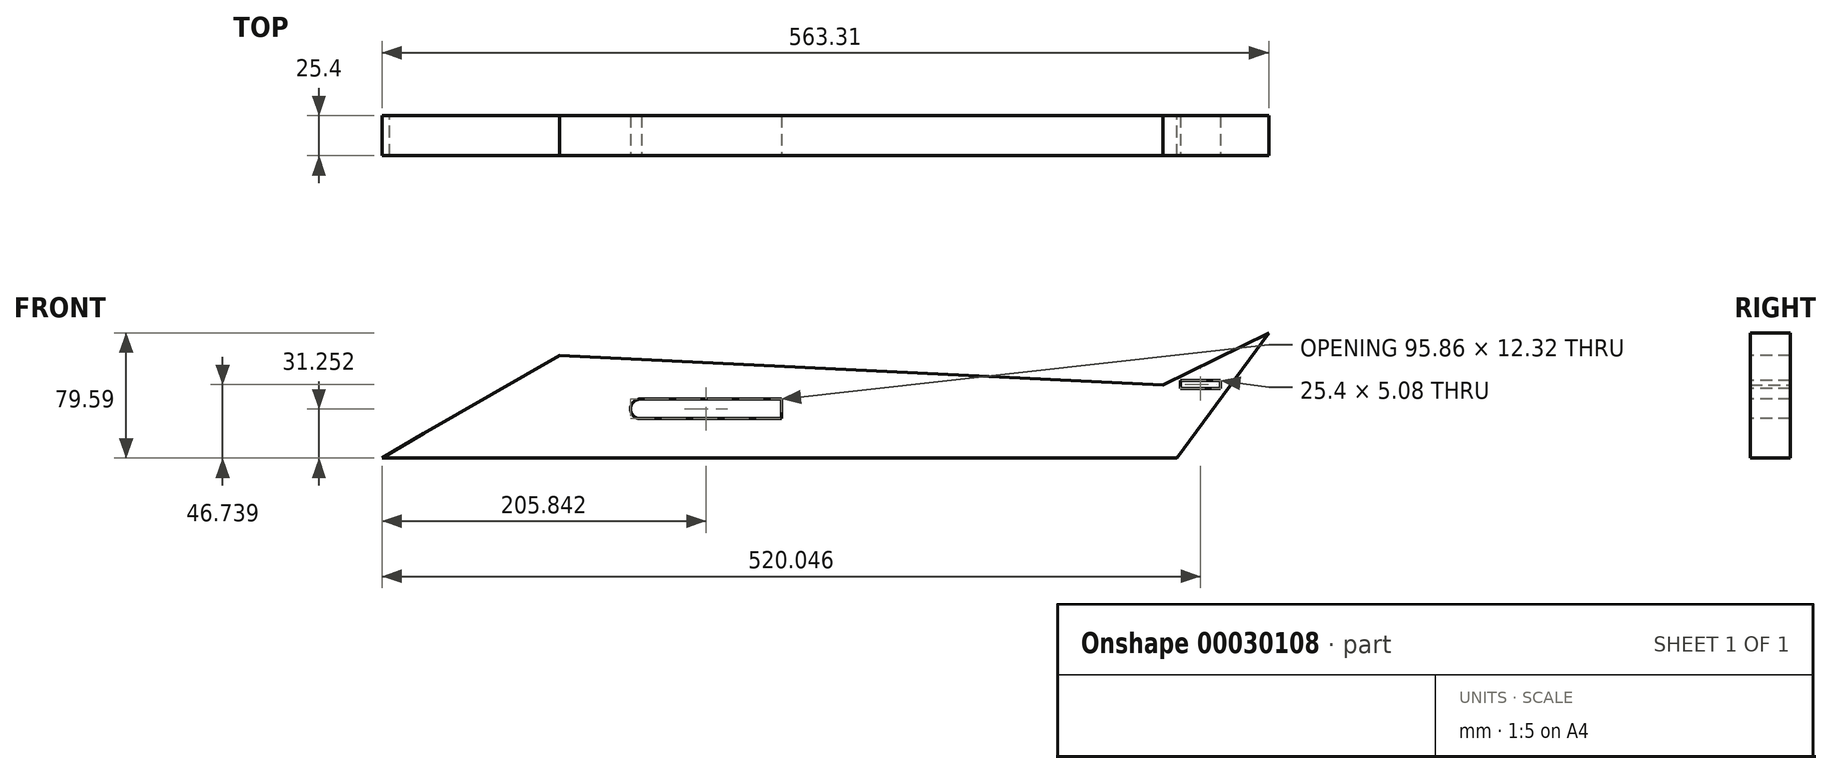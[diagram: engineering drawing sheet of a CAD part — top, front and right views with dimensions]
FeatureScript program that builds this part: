
annotation { "Feature Type Name" : "Feature", "Feature Type Description" : "" }
export const myFeature = defineFeature(function(context is Context, id is Id, definition is map)
    precondition{}
    {
        {
            var Q0;
            Q0=qCreatedBy(makeId("Front.planeOp"),FACE);
            var sketch = newSketch(context, id + "F0", { "sketchPlane" : qUnion([Q0])});
            skLineSegment(sketch, "E0", {"start": v(-248.94, -25.05) * mm, "end": v(251.06, -25.05) * mm});
            skLineSegment(sketch, "E1", {"start": v(251.06, -25.05) * mm, "end": v(309.54, 54.5) * mm});
            skLineSegment(sketch, "E2", {"start": v(309.54, 54.5) * mm, "end": v(242.29, 21.36) * mm});
            skLineSegment(sketch, "E3", {"start": v(242.29, 21.36) * mm, "end": v(-248.94, 45.48) * mm});
            skArc(sketch, "E4", {"start": v(-248.94, 45.48) * mm, "mid": v(-285.98, 10.21) * mm, "end": v(-248.94, -25.05) * mm});
            skSolve(sketch);
        }
        {
            var Q0;
            Q0=makeQuery(id+"F0.imprint","IMPRINT",FACE,{"disambiguationData":[TD([[makeQuery(id+"F0.imprint","IMPRINT",EDGE,{"derivedFrom":sQuery(id+"F0.wireOp",EDGE,"E0")}),1.0]])]});
            extrude(context, id + "F1", {"entities" : qUnion([Q0]), "depth" : 25.4 * mm});
        }
        {
            var Q0;
            Q0 = qSketchRegion(id + "F0", true);
            extrude(context, id + "F2", {"entities" : qUnion([Q0]), "operationType" : NewBodyOperationType.ADD, "depth" : 25.4 * mm});
        }
        {
            var Q0;
            Q0 = qSketchRegion(id + "F0", true);
            extrude(context, id + "F3", {"entities" : qUnion([Q0]), "operationType" : NewBodyOperationType.ADD, "depth" : 25.4 * mm});
        }
        {
            var Q0;
            Q0=makeQuery(id+"F1.opExtrude","CAP_FACE",FACE,{"disambiguationData":[OSD([sQuery(id+"F0.wireOp",EDGE,"E0"),sQuery(id+"F0.wireOp",EDGE,"E1"),sQuery(id+"F0.wireOp",EDGE,"E2"),sQuery(id+"F0.wireOp",EDGE,"E3"),sQuery(id+"F0.wireOp",EDGE,"E4")])],"isStart":false});
            var sketch = newSketch(context, id + "F4", { "sketchPlane" : qUnion([Q0])});
            skLineSegment(sketch, "E5", {"start": v(-88.78, 0) * mm, "end": v(0, 0) * mm});
            skLineSegment(sketch, "E6", {"start": v(0, 0) * mm, "end": v(-88.78, 12.32) * mm});
            skArc(sketch, "E7", {"start": v(-88.78, 12.32) * mm, "mid": v(-95.86, 6.16) * mm, "end": v(-88.78, 0) * mm});
            skSolve(sketch);
        }
        {
            var Q0;
            Q0=makeQuery(id+"F4.imprint","IMPRINT",FACE,{"disambiguationData":[TD([[makeQuery(id+"F4.imprint","IMPRINT",EDGE,{"derivedFrom":sQuery(id+"F4.wireOp",EDGE,"E5")}),1.0]])]});
            extrude(context, id + "F5", {"entities" : qUnion([Q0]), "operationType" : NewBodyOperationType.REMOVE, "oppositeDirection" : true, "depth" : 25.4 * mm});
        }
        {
            var Q0;
            Q0=makeQuery(id+"F1.opExtrude","CAP_FACE",FACE,{"disambiguationData":[OSD([sQuery(id+"F0.wireOp",EDGE,"E0"),sQuery(id+"F0.wireOp",EDGE,"E1"),sQuery(id+"F0.wireOp",EDGE,"E2"),sQuery(id+"F0.wireOp",EDGE,"E3"),sQuery(id+"F0.wireOp",EDGE,"E4")])],"isStart":false});
            var sketch = newSketch(context, id + "F6", { "sketchPlane" : qUnion([Q0])});
            skLineSegment(sketch, "E8", {"start": v(-88.78, 12.32) * mm, "end": v(-88.78, 0) * mm});
            skLineSegment(sketch, "E9", {"start": v(-88.78, 12.32) * mm, "end": v(0, 12.32) * mm});
            skLineSegment(sketch, "E10", {"start": v(0, 12.32) * mm, "end": v(0, 0) * mm});
            skSolve(sketch);
        }
        {
            var Q0;
            Q0 = qSketchRegion(id + "F6", true);
            var Q1;
            Q1=makeQuery(id+"F6.imprint","IMPRINT",FACE,{"disambiguationData":[TD([[makeQuery(id+"F6.imprint","IMPRINT",EDGE,{"derivedFrom":sQuery(id+"F6.wireOp",EDGE,"E8")}),1.0]])]});
            var Q2;
            Q2=makeQuery(id+"F6.imprint","IMPRINT",FACE,{"disambiguationData":[TD([[makeQuery(id+"F6.imprint","IMPRINT",EDGE,{"derivedFrom":sQuery(id+"F6.wireOp",EDGE,"E9")}),-1.0]])]});
            extrude(context, id + "F7", {"entities" : qUnion([Q0, Q1, Q2]), "operationType" : NewBodyOperationType.REMOVE, "oppositeDirection" : true, "depth" : 25.4 * mm});
        }
        {
            var Q0;
            Q0=makeQuery(id+"F1.opExtrude","CAP_FACE",FACE,{"disambiguationData":[OSD([sQuery(id+"F0.wireOp",EDGE,"E0"),sQuery(id+"F0.wireOp",EDGE,"E1"),sQuery(id+"F0.wireOp",EDGE,"E2"),sQuery(id+"F0.wireOp",EDGE,"E3"),sQuery(id+"F0.wireOp",EDGE,"E4")])],"isStart":false});
            var sketch = newSketch(context, id + "F8", { "sketchPlane" : qUnion([Q0])});
            skLineSegment(sketch, "E11", {"start": v(-88.78, 12.32) * mm, "end": v(-88.78, 0) * mm});
            skSolve(sketch);
        }
        {
            var Q0;
            Q0 = qSketchRegion(id + "F8", true);
            var Q1;
            Q1=makeQuery(id+"F8.imprint","IMPRINT",FACE,{"disambiguationData":[TD([[makeQuery(id+"F8.imprint","IMPRINT",EDGE,{"derivedFrom":sQuery(id+"F8.wireOp",EDGE,"E11")}),-1.0]])]});
            extrude(context, id + "F9", {"entities" : qUnion([Q0, Q1]), "depth" : 25.4 * mm});
        }
        {
            var Q0;
            Q0=makeQuery(id+"F9.opExtrude","CAP_FACE",FACE,{"disambiguationData":[OSD([sQuery(id+"F4.wireOp",EDGE,"E7"),sQuery(id+"F8.wireOp",EDGE,"E11")])],"isStart":false});
            extrude(context, id + "F10", {"entities" : qUnion([Q0]), "operationType" : NewBodyOperationType.REMOVE, "oppositeDirection" : true, "depth" : 25.4 * mm});
        }
        {
            var Q0;
            Q0=makeQuery(id+"F1.opExtrude","CAP_FACE",FACE,{"disambiguationData":[OSD([sQuery(id+"F0.wireOp",EDGE,"E0"),sQuery(id+"F0.wireOp",EDGE,"E1"),sQuery(id+"F0.wireOp",EDGE,"E2"),sQuery(id+"F0.wireOp",EDGE,"E3"),sQuery(id+"F0.wireOp",EDGE,"E4")])],"isStart":false});
            var sketch = newSketch(context, id + "F11", { "sketchPlane" : qUnion([Q0])});
            skLineSegment(sketch, "E12.bottom", {"start": v(-88.78, -10.1) * mm, "end": v(-110.2, -10.1) * mm});
            skLineSegment(sketch, "E12.top", {"start": v(-88.78, 19.23) * mm, "end": v(-110.2, 19.23) * mm});
            skLineSegment(sketch, "E12.left", {"start": v(-88.78, -10.1) * mm, "end": v(-88.78, 19.23) * mm});
            skLineSegment(sketch, "E12.right", {"start": v(-110.2, -10.1) * mm, "end": v(-110.2, 19.23) * mm});
            skSolve(sketch);
        }
        {
            var Q0;
            {var subQ0=makeQuery(id+"F5.boolean.opBoolean","COPY",EDGE,{"derivedFrom":makeQuery(id+"F5.opExtrude","CAP_EDGE",EDGE,{"disambiguationData":[OSD([sQuery(id+"F4.wireOp",EDGE,"E7")])],"isStart":true})});Q0=makeQuery(id+"F11.imprint","IMPRINT",FACE,{"disambiguationData":[TD([[makeQuery(id+"F11.imprint","IMPRINT",EDGE,{"derivedFrom":subQ0}),1.0]])]});}
            var Q1;
            {var subQ1=sQuery(id+"F11.wireOp",EDGE,"E12.bottom");Q1=makeQuery(id+"F11.imprint","IMPRINT",FACE,{"disambiguationData":[TD([[makeQuery(id+"F11.imprint","IMPRINT",EDGE,{"derivedFrom":subQ1}),-1.0]])]});}
            extrude(context, id + "F12", {"entities" : qUnion([Q0, Q1]), "operationType" : NewBodyOperationType.ADD, "oppositeDirection" : true, "depth" : 25.4 * mm});
        }
        {
            var Q0;
            Q0=makeQuery(id+"F12.boolean.opBoolean","MERGE",FACE,{"derivedFrom":[makeQuery(id+"F1.opExtrude","CAP_FACE",FACE,{"disambiguationData":[OSD([sQuery(id+"F0.wireOp",EDGE,"E0"),sQuery(id+"F0.wireOp",EDGE,"E1"),sQuery(id+"F0.wireOp",EDGE,"E2"),sQuery(id+"F0.wireOp",EDGE,"E3"),sQuery(id+"F0.wireOp",EDGE,"E4")])],"isStart":false}),makeQuery(id+"F12.opExtrude","CAP_FACE",FACE,{"disambiguationData":[OSD([sQuery(id+"F11.wireOp",EDGE,"E12.bottom"),sQuery(id+"F11.wireOp",EDGE,"E12.top"),sQuery(id+"F11.wireOp",EDGE,"E12.left"),sQuery(id+"F11.wireOp",EDGE,"E12.right")])],"isStart":true})]});
            var sketch = newSketch(context, id + "F13", { "sketchPlane" : qUnion([Q0])});
            skLineSegment(sketch, "E13", {"start": v(-248.94, -25.05) * mm, "end": v(-130.9, 39.68) * mm});
            skSolve(sketch);
        }
        {
            var Q0;
            Q0=makeQuery(id+"F1.opExtrude","CAP_FACE",FACE,{"disambiguationData":[OSD([sQuery(id+"F0.wireOp",EDGE,"E0"),sQuery(id+"F0.wireOp",EDGE,"E1"),sQuery(id+"F0.wireOp",EDGE,"E2"),sQuery(id+"F0.wireOp",EDGE,"E3"),sQuery(id+"F0.wireOp",EDGE,"E4")])],"isStart":false});
            var sketch = newSketch(context, id + "F14", { "sketchPlane" : qUnion([Q0])});
            skSolve(sketch);
        }
        {
            var Q0;
            {var subQ1=sQuery(id+"F13.wireOp",EDGE,"E13");Q0=makeQuery(id+"F13.imprint","IMPRINT",FACE,{"disambiguationData":[TD([[makeQuery(id+"F13.imprint","IMPRINT",EDGE,{"derivedFrom":subQ1}),1.0]])]});}
            extrude(context, id + "F15", {"entities" : qUnion([Q0]), "operationType" : NewBodyOperationType.ADD, "depth" : 25.4 * mm});
        }
        {
            var Q0;
            Q0=makeQuery(id+"F15.opExtrude","CAP_FACE",FACE,{"disambiguationData":[OSD([sQuery(id+"F0.wireOp",EDGE,"E3"),sQuery(id+"F0.wireOp",EDGE,"E4"),sQuery(id+"F13.wireOp",EDGE,"E13")])],"isStart":false});
            extrude(context, id + "F16", {"entities" : qUnion([Q0]), "operationType" : NewBodyOperationType.REMOVE, "oppositeDirection" : true, "depth" : 25.4 * mm});
        }
        {
            var Q0;
            Q0=makeQuery(id+"F14.imprint","IMPRINT",FACE,{"disambiguationData":[TD([[makeQuery(id+"F14.imprint","IMPRINT",EDGE,{"derivedFrom":makeQuery(id+"F1.opExtrude","CAP_EDGE",EDGE,{"disambiguationData":[OSD([sQuery(id+"F0.wireOp",EDGE,"E0")])],"isStart":false})}),1.0]])]});
            var sketch = newSketch(context, id + "F17", { "sketchPlane" : qUnion([Q0])});
            skLineSegment(sketch, "E14", {"start": v(-255.34, -25.8) * mm, "end": v(-138.7, 41.46) * mm});
            skLineSegment(sketch, "E15", {"start": v(-138.7, 41.46) * mm, "end": v(-278.67, 55.02) * mm});
            skLineSegment(sketch, "E16", {"start": v(-278.67, 55.02) * mm, "end": v(-310.47, -22.74) * mm});
            skLineSegment(sketch, "E17", {"start": v(-310.47, -22.74) * mm, "end": v(-255.34, -25.8) * mm});
            skSolve(sketch);
        }
        {
            var Q0;
            Q0 = qSketchRegion(id + "F17", true);
            extrude(context, id + "F18", {"entities" : qUnion([Q0]), "operationType" : NewBodyOperationType.REMOVE, "oppositeDirection" : true, "depth" : 25.4 * mm});
        }
        {
            var Q0;
            Q0=makeQuery(id+"F14.imprint","IMPRINT",FACE,{"disambiguationData":[TD([[makeQuery(id+"F14.imprint","IMPRINT",EDGE,{"derivedFrom":makeQuery(id+"F1.opExtrude","CAP_EDGE",EDGE,{"disambiguationData":[OSD([sQuery(id+"F0.wireOp",EDGE,"E0")])],"isStart":false})}),1.0]])]});
            var sketch = newSketch(context, id + "F19", { "sketchPlane" : qUnion([Q0])});
            skLineSegment(sketch, "E18", {"start": v(-141.27, 40.17) * mm, "end": v(-265.6, -31.81) * mm});
            skLineSegment(sketch, "E19", {"start": v(-265.6, -31.81) * mm, "end": v(-321.3, 3.47) * mm});
            skLineSegment(sketch, "E20", {"start": v(-321.3, 3.47) * mm, "end": v(-274.7, 68.86) * mm});
            skLineSegment(sketch, "E21", {"start": v(-274.7, 68.86) * mm, "end": v(-141.27, 40.17) * mm});
            skSolve(sketch);
        }
        {
            var Q0;
            Q0 = qSketchRegion(id + "F19", true);
            extrude(context, id + "F20", {"entities" : qUnion([Q0]), "operationType" : NewBodyOperationType.REMOVE, "oppositeDirection" : true, "depth" : 25.4 * mm});
        }
        {
            var Q0;
            Q0=makeQuery(id+"F14.imprint","IMPRINT",FACE,{"disambiguationData":[TD([[makeQuery(id+"F14.imprint","IMPRINT",EDGE,{"derivedFrom":makeQuery(id+"F1.opExtrude","CAP_EDGE",EDGE,{"disambiguationData":[OSD([sQuery(id+"F0.wireOp",EDGE,"E0")])],"isStart":false})}),1.0]])]});
            var sketch = newSketch(context, id + "F21", { "sketchPlane" : qUnion([Q0])});
            skLineSegment(sketch, "E22", {"start": v(278.98, 19.1) * mm, "end": v(253.58, 19.1) * mm});
            skLineSegment(sketch, "E23", {"start": v(253.58, 19.1) * mm, "end": v(253.58, 24.19) * mm});
            skLineSegment(sketch, "E24", {"start": v(253.58, 24.19) * mm, "end": v(278.98, 24.19) * mm});
            skLineSegment(sketch, "E25", {"start": v(278.98, 24.19) * mm, "end": v(278.98, 19.1) * mm});
            skSolve(sketch);
        }
        {
            var Q0;
            Q0=makeQuery(id+"F21.imprint","IMPRINT",FACE,{"disambiguationData":[TD([[makeQuery(id+"F21.imprint","IMPRINT",EDGE,{"derivedFrom":sQuery(id+"F21.wireOp",EDGE,"E22")}),-1.0]])]});
            extrude(context, id + "F22", {"entities" : qUnion([Q0]), "operationType" : NewBodyOperationType.REMOVE, "oppositeDirection" : true, "depth" : 25.4 * mm});
        }
    });
